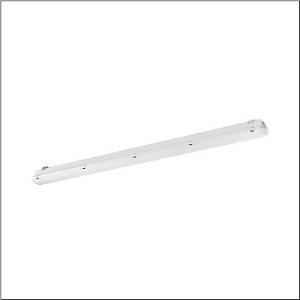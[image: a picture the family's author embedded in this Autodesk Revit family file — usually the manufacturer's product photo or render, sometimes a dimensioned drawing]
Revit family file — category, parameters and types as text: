
# Revit family: monsun_11xtreme_mo_51fe10mp480s
name_source: partatom
category: Lighting Fixtures
units: mm (PartAtom-declared; Revit-internal decimal feet)

## family parameters
Cut with Voids When Loaded = No
Host = Face
Light Source = No
Part Type = Normal
Room Calculation Point = No
Round Connector Dimension = Use Diameter
Shared = No

## types (1)
- --- (1 x LED, 8000 lm, 40.1 W, 4000K)
    Apparent Load = 40 VA
    CIE Flux Codes = 47 77 93 94 100
    Color Rendering = 80
    Color Temperature = 4000K
    Default Elevation = 1800 mm
    Description = Monsun 11Xtreme MO, damp-proof luminaire, chain hanger, primary optical cover: enclosure, of PMMA, light emission: direct distribution, primary light characteristic: symmetric, installation type: suspended mounting, surface-mounted, horizontal mounting, vertical mounting, LED, rated luminous flux: 8.000lm, luminous efficacy: 200lm/W, light colour: 840, colour temperature: 4000K, control gear: ON/OFF Multilumen, with terminal, 3-pole, max. 2.5mm², mains connection: 220..240V, AC, 50/60Hz, rated input power: 40W, luminaire housing, of glass-fibre reinforced polyester, uncoated, bright grey, incl. chain hanger, length: 1.590mm, width: 90mm, height: 88mm, clip for enclosure, of stainless steel (V2A), ceiling mounting element, of stainless steel (V2A), chain hanger, of stainless steel (V2A), protection rating (complete): IP66, insulation class (complete): insulation class I (protective earthing), certification: CE, ENEC, VDE, UKCA, protection symbol: D, impact resistance: IK04, permissible operating ambient temperature: -35..+45°C, standard: EN 50419, EN 60598-2-1, contact your sales advisor before using the luminaires in applications with unclear chemical exposure, large temperature fluctuations or condensation-forming humidity, LABS conformity tested according to VDMA 24364:2018-05, no direct snow, no direct sun, no direct rain, for indoor or canopied outdoor use, corresponds to IFS (International Featured Standards) requirements for safety and quality in the food industry, packaging unit: 1 piece
    Height = 88 mm
    Lamp = 1 x LED
    Lamp Light Flux = 8000 lm
    Lamp Power = 40.1 W
    Lamp count = 1
    Length = 1590 mm
    Luminous efficacy = 200 lm/W
    Manufacturer = Siteco
    ModVariant = No
    Model = 51FE10MP480S
    Mounting Place = Ceiling
    Mounting Type = Surface mounted
    Number of Poles = 1
    OnlyDefault = Yes
    Power Factor = 1
    Product Name = Monsun 11Xtreme MO
    Product group = damp-proof luminaire
    ProductGroupID = 300
    Protection Class = Protection class I
    Protection Degree = IP 66
    RLX_Detail_Level = 1
    RLX_Emergency_Light_Flux = 0 lm
    RLX_Emergency_Type = 0
    RLX_Emergency_Type_DB = No
    RlxData = <blob elided: 84929 chars, md5=da68e2bf>
    Socket = socket
    Standby Power = 0 W
    System Light Flux = 8000 lm
    System Power = 40 W
    Type Comments = factory setting: luminous flux: 100 % | (A | C | E) | 95 mA
    Type Image = l_1349234.jpg
    URL = http://relux.com
    VarID = @adj_034435
    Voltage = 0 V
    Weight = 0.00 kg
    Width = 90 mm

## geometry (parser evidence)
native form markers: Blend x4, Sweep x13
no freeform markers — native parametric forms only
